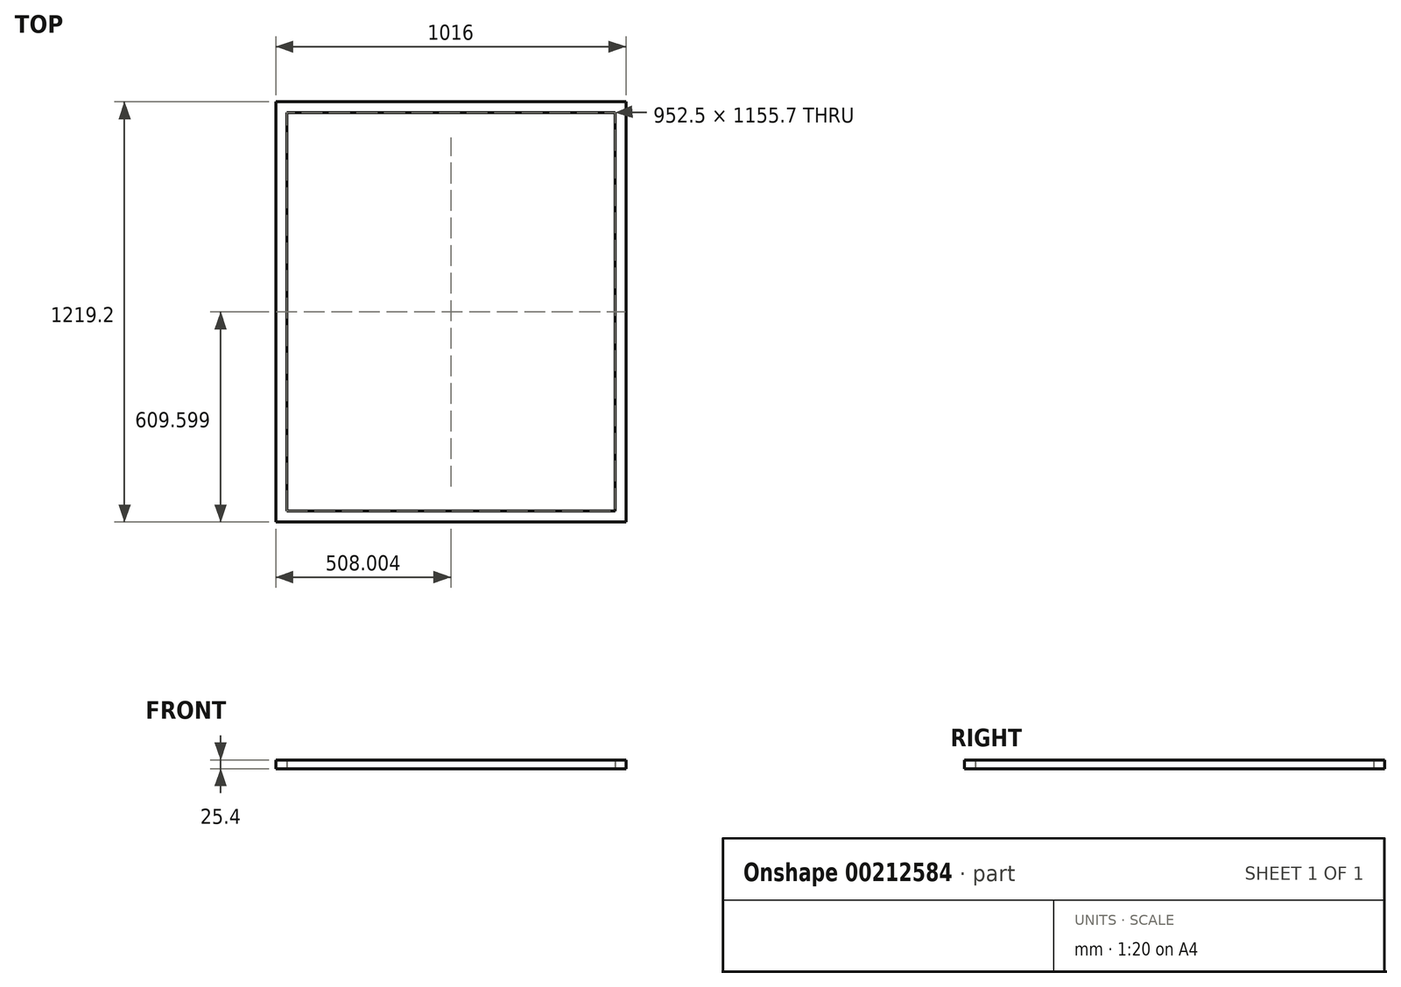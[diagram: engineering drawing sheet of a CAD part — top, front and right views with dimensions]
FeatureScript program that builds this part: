
annotation { "Feature Type Name" : "Feature", "Feature Type Description" : "" }
export const myFeature = defineFeature(function(context is Context, id is Id, definition is map)
    precondition{}
    {
        {
            var Q0;
            Q0=qCreatedBy(makeId("Top.planeOp"),FACE);
            var sketch = newSketch(context, id + "F0", { "sketchPlane" : qUnion([Q0])});
            skLineSegment(sketch, "E0.bottom", {"start": v(-371.79, 1098.63) * mm, "end": v(644.21, 1098.63) * mm});
            skLineSegment(sketch, "E0.top", {"start": v(-371.79, -120.57) * mm, "end": v(644.21, -120.57) * mm});
            skLineSegment(sketch, "E0.left", {"start": v(-371.79, 1098.63) * mm, "end": v(-371.79, -120.57) * mm});
            skLineSegment(sketch, "E0.right", {"start": v(644.21, 1098.63) * mm, "end": v(644.21, -120.57) * mm});
            skLineSegment(sketch, "E1.0", {"start": v(-340.04, 1066.88) * mm, "end": v(612.46, 1066.88) * mm});
            skLineSegment(sketch, "E1.1", {"start": v(-340.04, 1066.88) * mm, "end": v(-340.04, -88.82) * mm});
            skLineSegment(sketch, "E1.2", {"start": v(-340.04, -88.82) * mm, "end": v(612.46, -88.82) * mm});
            skLineSegment(sketch, "E1.3", {"start": v(612.46, 1066.88) * mm, "end": v(612.46, -88.82) * mm});
            skCircle(sketch, "E2", {"center": v(109.95, 497.52) * mm, "radius": 38.06 * mm});
            skSolve(sketch);
        }
        {
            var Q0;
            Q0 = qSketchRegion(id + "F0", true);
            extrude(context, id + "F1", {"entities" : qUnion([Q0]), "depth" : 25.4 * mm});
        }
    });
